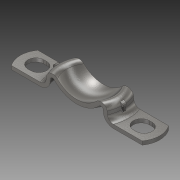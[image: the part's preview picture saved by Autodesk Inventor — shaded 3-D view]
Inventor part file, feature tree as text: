
AUTODESK INVENTOR PART (.ipt)
format: ipt  version: 2018 (Build 220112000, 112)  size: 289,792 bytes
history: native  units: in
note: dims shown in document units (in); Inventor stores cm internally (conversion verified against a paired STEP export)
features: mirror x1
ambient origin geometry x8: Origin, YZ Plane, XZ Plane, XY Plane, X Axis, Y Axis, Z Axis, Center Point
bodies: Solid1 (feature_tree)
feature tree (1):
  mirror  "Mirror1"
